# Revit family: NBS_Allermuir_DmstcChrs_Mote_MTE-MED01
name_source: partatom
category: Furniture
revit_build: Autodesk Revit 2016 (Build: 20161004_0715(x64)
units: mm (PartAtom-declared; Revit-internal decimal feet)

## family parameters
Always vertical = Yes
Cut with Voids When Loaded = No
Room Calculation Point = No
Shared = No
Work Plane-Based = No

## types (1)
- MTE-MED01
    AssetType = Moveable
    BIMObjectName = NBS_Allermuir_DomesticChairs_Mote_MTE-MED01
    Category = Pr_40_50_12_22:Dining chairs
    Depth = 750 mm  [stored 2.46063 ft]
    Description = Media panel
    DurationUnit = year
    ExpectedLife = 5
    Features = Fully upholstered, screen fixing brackets
    HasLeftSideScreen = Yes
    HasRightSideScreen = Yes
    HasScreens = Yes
    HighestSeatingHeight = 0 mm  [stored 0 ft]
    IfcExportAs = IfcFurnitureType
    IfcExportType = SOFA
    IsBuiltIn = No
    JoiningArmOffset = 15 mm  [stored 0.0492126 ft]
    LowestSeatingHeight = 0 mm  [stored 0 ft]
    ManufacturerName = Allermuir
    ManufacturerURL = http://www.thesenatorgroup.com
    ModelNumber = MTE-MED01
    ModelReference = Mote accessories
    NBSCertification = www.nationalbimlibrary.com/cert/m3oawnli
    NBSDescription = Domestic chairs
    NBSReference = 45-35-20/365
    Name = DomesticChairs_Mote_MTE-MED01_Allermuir
    NominalDepth = 1260 mm
    NominalHeight = 1030 mm  [stored 3.37927 ft]
    NominalLength = 0 mm  [stored 0 ft]
    NominalWidth = 1260 mm
    OverallWidth = 2245 mm  [stored 7.36549 ft]
    ProductInformation = http://www.thesenatorgroup.com
    ScreenFinishMaterial = NBS_Concept
    ScreenHeight = 1030 mm  [stored 3.37927 ft]
    ScreenHeightPosition = 1325 mm  [stored 4.34711 ft]
    ScreenLength = 1274 mm  [stored 4.17979 ft]
    ScreenWidth = 44 mm  [stored 0.144357 ft]
    SeatFrameMaterial = NBS_Concept
    SeatingHeight = 0 mm  [stored 0 ft]
    SeatsAndBacksMaterial = Upholstered
    ShowLeftSideScreen = Yes
    ShowRightSideScreen = Yes
    Size = 0
    Status = UNSET
    Uniclass2015Code = Pr_40_50_12_22
    Uniclass2015Title = Dining chairs
    Uniclass2015Version = Products v1.9
    Version = 1
    WarrantyDescription = Allermuir warrant that its manufactured products are free from manufacturing defects in materials or workmanship for a period of five years
    WarrantyDurationParts = 5
    WarrantyDurationUnit = year

note: [stored X ft] marks values corroborated as IEEE doubles in the binary element streams (Revit-internal decimal feet)

## geometry (parser evidence)
native form markers: Sweep x2
no freeform markers — native parametric forms only
